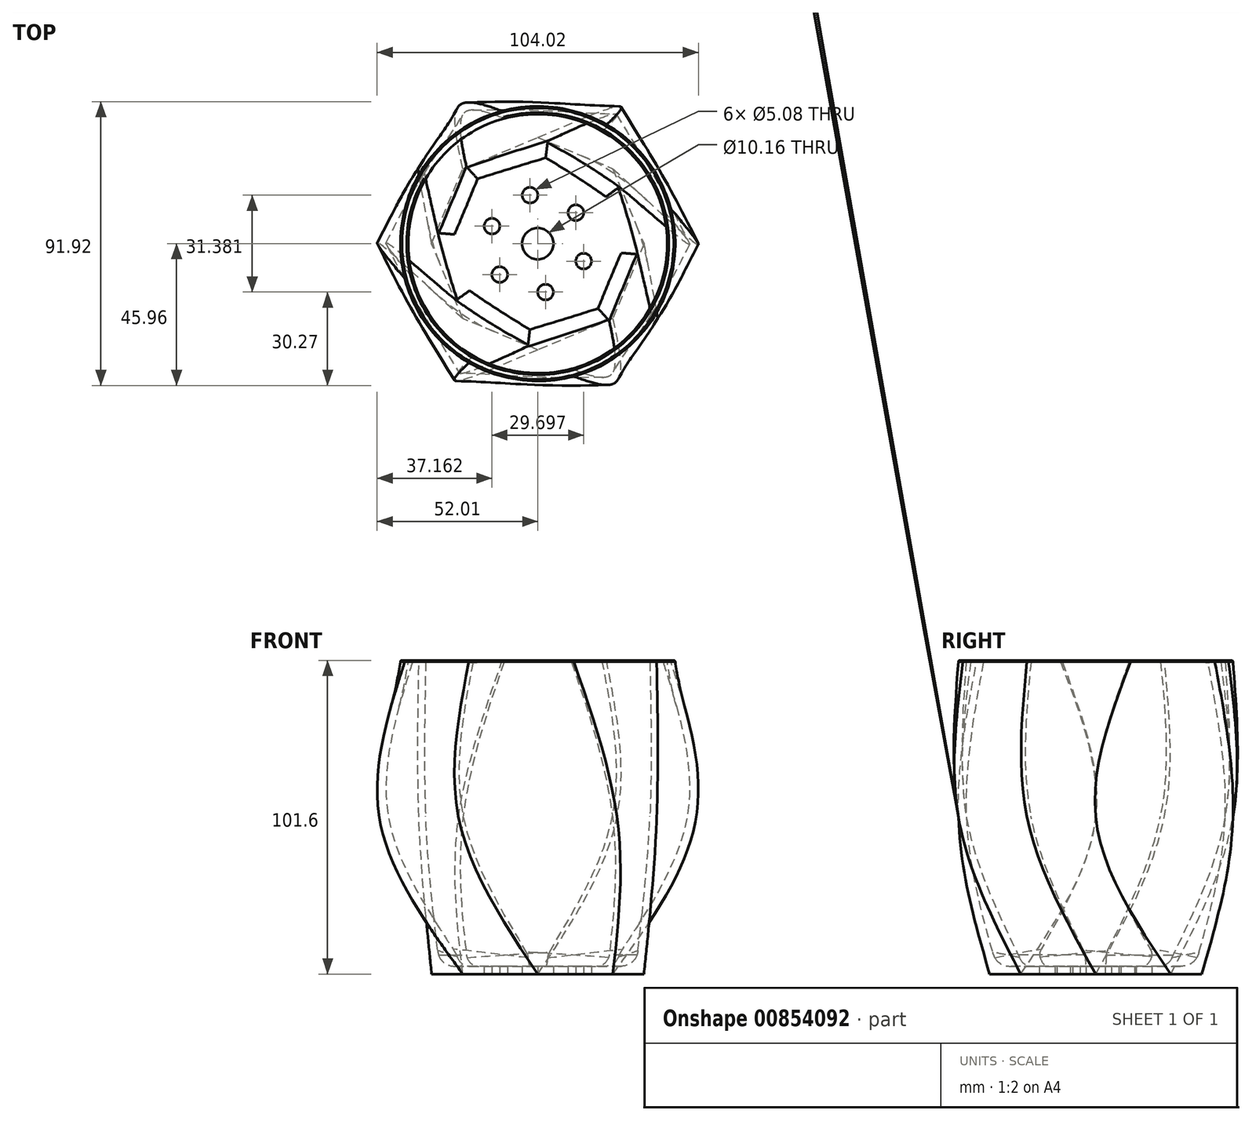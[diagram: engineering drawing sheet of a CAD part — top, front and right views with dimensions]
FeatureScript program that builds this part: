
annotation { "Feature Type Name" : "Feature", "Feature Type Description" : "" }
export const myFeature = defineFeature(function(context is Context, id is Id, definition is map)
    precondition{}
    {
        {
            var Q0;
            Q0=qCreatedBy(makeId("Top.planeOp"),FACE);
            var sketch = newSketch(context, id + "F0", { "sketchPlane" : qUnion([Q0])});
            skCircle(sketch, "E0.cCircle", {"center": v(0, 0) * mm, "radius": 31.75 * mm, "construction": true});
            skLineSegment(sketch, "E0.0", {"start": v(0, 34.37) * mm, "end": v(24.3, 24.3) * mm});
            skLineSegment(sketch, "E0.1", {"start": v(24.3, 24.3) * mm, "end": v(34.37, 0) * mm});
            skLineSegment(sketch, "E0.2", {"start": v(34.37, 0) * mm, "end": v(24.3, -24.3) * mm});
            skLineSegment(sketch, "E0.3", {"start": v(24.3, -24.3) * mm, "end": v(0, -34.37) * mm});
            skLineSegment(sketch, "E0.4", {"start": v(0, -34.37) * mm, "end": v(-24.3, -24.3) * mm});
            skLineSegment(sketch, "E0.5", {"start": v(-24.3, -24.3) * mm, "end": v(-34.37, 0) * mm});
            skLineSegment(sketch, "E0.6", {"start": v(-34.37, 0) * mm, "end": v(-24.3, 24.3) * mm});
            skLineSegment(sketch, "E0.7", {"start": v(-24.3, 24.3) * mm, "end": v(0, 34.37) * mm});
            skPoint(sketch, "E0.0.midPoint", {"position": v(12.15, 29.33) * mm});
            skSolve(sketch);
        }
        {
            var Q0;
            Q0=qCreatedBy(makeId("Top.planeOp"),FACE);
            cPlane(context, id + "F1", {"entities" : qUnion([Q0]), "cplaneType" : CPlaneType.OFFSET, "offset" : 50.8 * mm, "width" : 152.4 * mm, "height" : 152.4 * mm});
        }
        {
            var Q0;
            Q0=qCreatedBy(id+"F1.planeOp",FACE);
            var sketch = newSketch(context, id + "F2", { "sketchPlane" : qUnion([Q0])});
            skCircle(sketch, "E1.cCircle", {"center": v(0, 0) * mm, "radius": 44.45 * mm, "construction": true});
            skLineSegment(sketch, "E1.0", {"start": v(25.66, -44.45) * mm, "end": v(-25.66, -44.45) * mm});
            skLineSegment(sketch, "E1.1", {"start": v(-25.66, -44.45) * mm, "end": v(-51.33, 0) * mm});
            skLineSegment(sketch, "E1.2", {"start": v(-51.33, 0) * mm, "end": v(-25.66, 44.45) * mm});
            skLineSegment(sketch, "E1.3", {"start": v(-25.66, 44.45) * mm, "end": v(25.66, 44.45) * mm});
            skLineSegment(sketch, "E1.4", {"start": v(25.66, 44.45) * mm, "end": v(51.33, 0) * mm});
            skLineSegment(sketch, "E1.5", {"start": v(51.33, 0) * mm, "end": v(25.66, -44.45) * mm});
            skPoint(sketch, "E1.0.midPoint", {"position": v(0, -44.45) * mm});
            skSolve(sketch);
        }
        {
            var Q0;
            Q0=qCreatedBy(id+"F1.planeOp",FACE);
            cPlane(context, id + "F3", {"entities" : qUnion([Q0]), "cplaneType" : CPlaneType.OFFSET, "offset" : 50.8 * mm, "width" : 152.4 * mm, "height" : 152.4 * mm});
        }
        {
            var Q0;
            Q0=qCreatedBy(id+"F3.planeOp",FACE);
            var sketch = newSketch(context, id + "F4", { "sketchPlane" : qUnion([Q0])});
            skCircle(sketch, "E2", {"center": v(0, 0) * mm, "radius": 44.45 * mm});
            skSolve(sketch);
        }
        {
            var Q0;
            Q0=makeQuery(id+"F0.imprint","IMPRINT",FACE,{"disambiguationData":[TD([[makeQuery(id+"F0.imprint","IMPRINT",EDGE,{"derivedFrom":sQuery(id+"F0.wireOp",EDGE,"E0.0")}),-1.0]])]});
            var Q1;
            Q1=makeQuery(id+"F2.imprint","IMPRINT",FACE,{"disambiguationData":[TD([[makeQuery(id+"F2.imprint","IMPRINT",EDGE,{"derivedFrom":sQuery(id+"F2.wireOp",EDGE,"E1.0")}),-1.0]])]});
            var Q2;
            Q2=makeQuery(id+"F4.imprint","IMPRINT",FACE,{"disambiguationData":[TD([[makeQuery(id+"F4.imprint","IMPRINT",EDGE,{"derivedFrom":sQuery(id+"F4.wireOp",EDGE,"E2")}),1.0]])]});
            loft(context, id + "F5", {"sheetProfilesArray" : [{ "sheetProfileEntities" : qUnion([Q0]) }, { "sheetProfileEntities" : qUnion([Q1]) }, { "sheetProfileEntities" : qUnion([Q2]) }]});
        }
        {
            var Q0;
            Q0=makeQuery(id+"F5.opLoft","CAP_FACE",FACE,{"disambiguationData":[OSD([makeQuery(id+"F4.imprint","IMPRINT",FACE,{"disambiguationData":[TD([[makeQuery(id+"F4.imprint","IMPRINT",EDGE,{"derivedFrom":sQuery(id+"F4.wireOp",EDGE,"E2")}),1.0]])]})])],"isStart":true});
            shell(context, id + "F6", {"entities" : qUnion([Q0]), "thickness" : 2.54 * mm});
        }
        {
            var Q0;
            Q0=makeQuery(id+"F5.opLoft","CAP_FACE",FACE,{"disambiguationData":[OSD([makeQuery(id+"F0.imprint","IMPRINT",FACE,{"disambiguationData":[TD([[makeQuery(id+"F0.imprint","IMPRINT",EDGE,{"derivedFrom":sQuery(id+"F0.wireOp",EDGE,"E0.0")}),-1.0]])]})])],"isStart":true});
            var sketch = newSketch(context, id + "F7", { "sketchPlane" : qUnion([Q0])});
            skCircle(sketch, "E3", {"center": v(0, 0) * mm, "radius": 5.08 * mm});
            skCircle(sketch, "E4", {"center": v(-12.33, 10.03) * mm, "radius": 2.54 * mm});
            skCircle(sketch, "E5.1.0", {"center": v(-14.85, -5.66) * mm, "radius": 2.54 * mm});
            skCircle(sketch, "E5.2.0", {"center": v(-2.52, -15.7) * mm, "radius": 2.54 * mm});
            skCircle(sketch, "E6.1.3.0", {"center": v(12.33, -10.03) * mm, "radius": 2.54 * mm});
            skCircle(sketch, "E6.1.4.0", {"center": v(14.85, 5.66) * mm, "radius": 2.54 * mm});
            skCircle(sketch, "E6.1.5.0", {"center": v(2.52, 15.7) * mm, "radius": 2.54 * mm});
            skSolve(sketch);
        }
        {
            var Q0;
            Q0 = qSketchRegion(id + "F7", true);
            extrude(context, id + "F8", {"entities" : qUnion([Q0]), "operationType" : NewBodyOperationType.REMOVE, "endBound" : BoundingType.THROUGH_ALL, "oppositeDirection" : true, "depth" : 25.4 * mm, "offsetDistance" : 25.4 * mm});
        }
        {
            var Q0;
            Q0=makeQuery(id+"F5.opLoft","CAP_FACE",FACE,{"disambiguationData":[OSD([makeQuery(id+"F4.imprint","IMPRINT",FACE,{"disambiguationData":[TD([[makeQuery(id+"F4.imprint","IMPRINT",EDGE,{"derivedFrom":sQuery(id+"F4.wireOp",EDGE,"E2")}),1.0]])]})])],"isStart":true});
            fillet(context, id + "F9", {"entities" : qUnion([Q0]), "radius" : 0.5 * mm, "tangentPropagation" : true, "allowEdgeOverflow" : false});
        }
        {
            var Q0;
            Q0=makeQuery(id+"F6.opShell","OFFSET_EDGE",EDGE,{"disambiguationData":[OSD([sQuery(id+"F0.wireOp",EDGE,"E0.3"),sQuery(id+"F0.wireOp",EDGE,"E0.4"),sQuery(id+"F0.wireOp",EDGE,"E0.5")])]});
            var Q1;
            Q1=makeQuery(id+"F6.opShell","OFFSET_EDGE",EDGE,{"disambiguationData":[OSD([sQuery(id+"F0.wireOp",EDGE,"E0.4"),sQuery(id+"F0.wireOp",EDGE,"E0.5"),sQuery(id+"F0.wireOp",EDGE,"E0.6")])]});
            var Q2;
            Q2=makeQuery(id+"F6.opShell","OFFSET_EDGE",EDGE,{"disambiguationData":[OSD([sQuery(id+"F0.wireOp",EDGE,"E0.5"),sQuery(id+"F0.wireOp",EDGE,"E0.6"),sQuery(id+"F0.wireOp",EDGE,"E0.7")])]});
            var Q3;
            Q3=makeQuery(id+"F6.opShell","OFFSET_EDGE",EDGE,{"disambiguationData":[OSD([sQuery(id+"F0.wireOp",EDGE,"E0.0"),sQuery(id+"F0.wireOp",EDGE,"E0.6"),sQuery(id+"F0.wireOp",EDGE,"E0.7")])]});
            var Q4;
            Q4=makeQuery(id+"F6.opShell","OFFSET_EDGE",EDGE,{"disambiguationData":[OSD([sQuery(id+"F0.wireOp",EDGE,"E0.0"),sQuery(id+"F0.wireOp",EDGE,"E0.1"),sQuery(id+"F0.wireOp",EDGE,"E0.7")])]});
            var Q5;
            Q5=makeQuery(id+"F6.opShell","OFFSET_EDGE",EDGE,{"disambiguationData":[OSD([sQuery(id+"F0.wireOp",EDGE,"E0.0"),sQuery(id+"F0.wireOp",EDGE,"E0.1"),sQuery(id+"F0.wireOp",EDGE,"E0.2")])]});
            var Q6;
            Q6=makeQuery(id+"F6.opShell","OFFSET_EDGE",EDGE,{"disambiguationData":[OSD([sQuery(id+"F0.wireOp",EDGE,"E0.1"),sQuery(id+"F0.wireOp",EDGE,"E0.2"),sQuery(id+"F0.wireOp",EDGE,"E0.3")])]});
            var Q7;
            Q7=makeQuery(id+"F6.opShell","OFFSET_EDGE",EDGE,{"disambiguationData":[OSD([sQuery(id+"F0.wireOp",EDGE,"E0.2"),sQuery(id+"F0.wireOp",EDGE,"E0.3"),sQuery(id+"F0.wireOp",EDGE,"E0.4")])]});
            fillet(context, id + "F10", {"entities" : qUnion([Q0, Q1, Q2, Q3, Q4, Q5, Q6, Q7]), "radius" : 5.08 * mm, "tangentPropagation" : true, "allowEdgeOverflow" : false});
        }
    });
